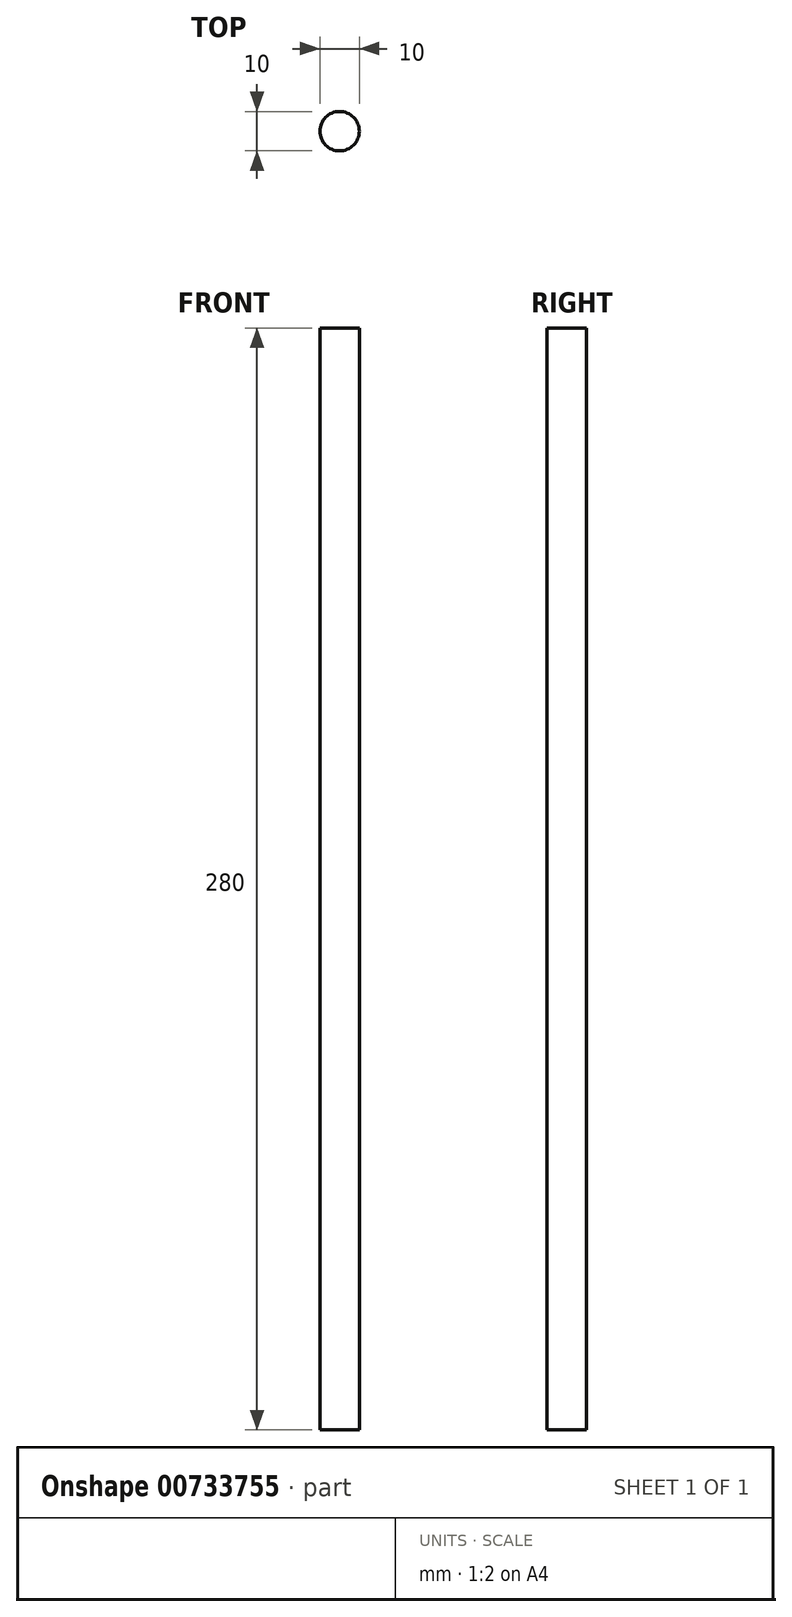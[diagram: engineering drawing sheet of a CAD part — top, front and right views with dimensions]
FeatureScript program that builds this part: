
annotation { "Feature Type Name" : "Feature", "Feature Type Description" : "" }
export const myFeature = defineFeature(function(context is Context, id is Id, definition is map)
    precondition{}
    {
        {
            var Q0;
            Q0=qCreatedBy(makeId("Top.planeOp"),FACE);
            var sketch = newSketch(context, id + "F0", { "sketchPlane" : qUnion([Q0])});
            skCircle(sketch, "E0", {"center": v(0, 0) * mm, "radius": 5 * mm});
            skSolve(sketch);
        }
        {
            var Q0;
            Q0=qSketchRegion(id+"F0",true);
            extrude(context, id + "F1", {"entities" : qUnion([Q0]), "depth" : 280 * mm, "offsetDistance" : 25 * mm});
        }
    });
